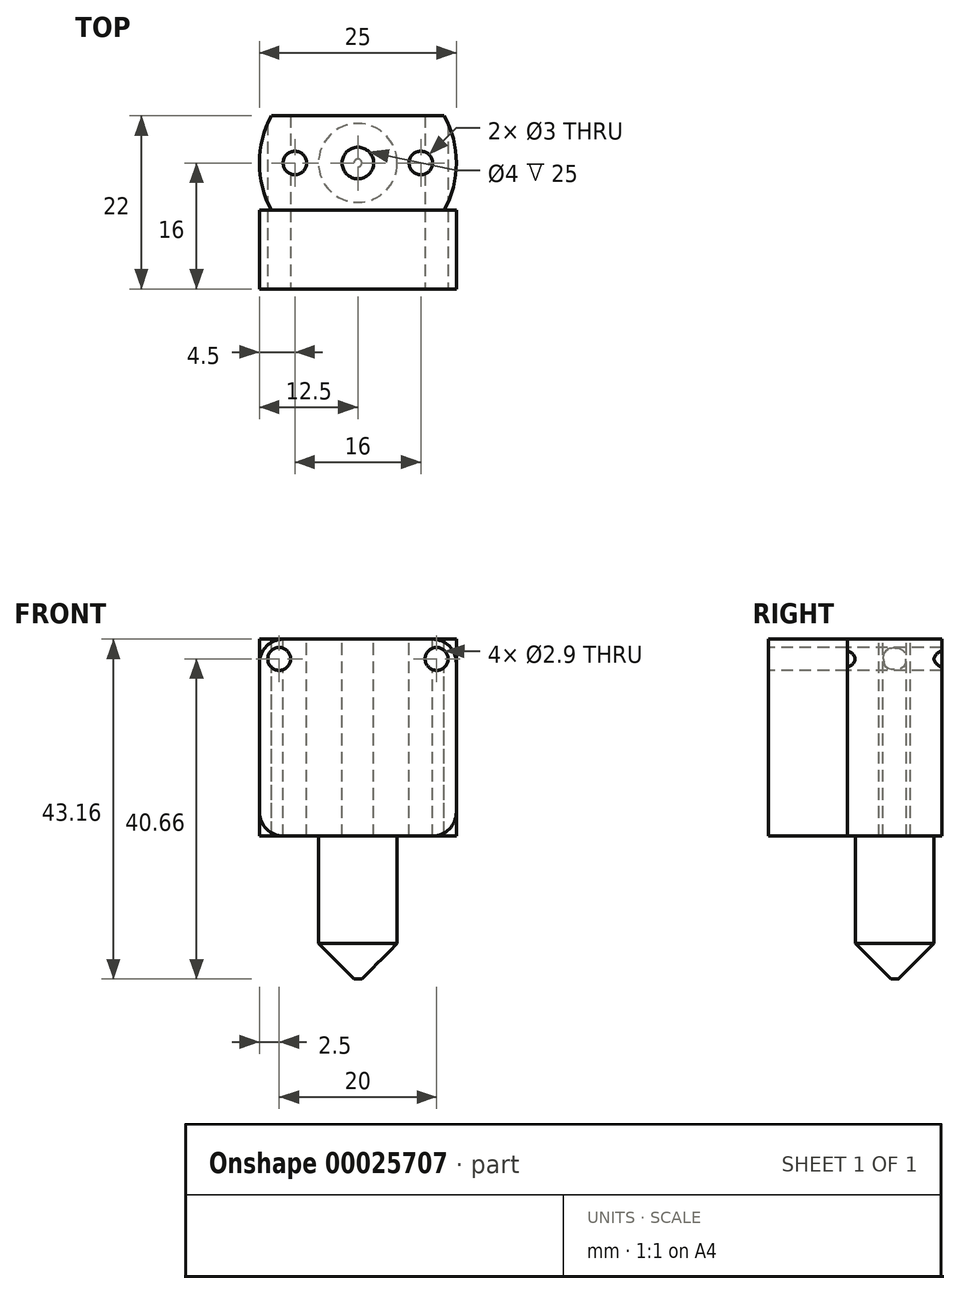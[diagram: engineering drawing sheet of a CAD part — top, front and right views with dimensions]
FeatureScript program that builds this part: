
annotation { "Feature Type Name" : "Feature", "Feature Type Description" : "" }
export const myFeature = defineFeature(function(context is Context, id is Id, definition is map)
    precondition{}
    {
        {
            var Q0;
            Q0=qCreatedBy(makeId("Front.planeOp"),FACE);
            var sketch = newSketch(context, id + "F0", { "sketchPlane" : qUnion([Q0])});
            skLineSegment(sketch, "E0.bottom", {"start": v(12.5, 0) * mm, "end": v(-12.5, 0) * mm});
            skLineSegment(sketch, "E0.top", {"start": v(12.5, -25) * mm, "end": v(-12.5, -25) * mm});
            skLineSegment(sketch, "E0.left", {"start": v(12.5, 0) * mm, "end": v(12.5, -25) * mm});
            skLineSegment(sketch, "E0.right", {"start": v(-12.5, 0) * mm, "end": v(-12.5, -25) * mm});
            skPoint(sketch, "E0.middle", {"position": v(0, -12.5) * mm});
            skSolve(sketch);
        }
        {
            var Q0;
            Q0 = qSketchRegion(id + "F0", true);
            extrude(context, id + "F1", {"entities" : qUnion([Q0]), "depth" : 12 * mm, "symmetric" : true});
        }
        {
            var Q0;
            Q0=qCreatedBy(makeId("Front.planeOp"),FACE);
            var sketch = newSketch(context, id + "F2", { "sketchPlane" : qUnion([Q0])});
            skLineSegment(sketch, "E1", {"start": v(0, -25) * mm, "end": v(0, -43.16) * mm});
            skLineSegment(sketch, "E2", {"start": v(0, -43.16) * mm, "end": v(0.5, -43.16) * mm});
            skLineSegment(sketch, "E3", {"start": v(0.5, -43.16) * mm, "end": v(5, -38.66) * mm});
            skLineSegment(sketch, "E4", {"start": v(5, -38.66) * mm, "end": v(5, -25) * mm});
            skLineSegment(sketch, "E5", {"start": v(5, -25) * mm, "end": v(0, -25) * mm});
            skSolve(sketch);
        }
        {
            var Q0;
            Q0 = qSketchRegion(id + "F2", true);
            var Q1;
            Q1=sQuery(id+"F2.wireOp",EDGE,"E1");
            revolve(context, id + "F3", {"operationType" : NewBodyOperationType.ADD, "entities" : qUnion([Q0]), "axis" : qUnion([Q1]), "revolveType" : RevolveType.FULL});
        }
        {
            var Q0;
            Q0=makeQuery(id+"F1.opExtrude","SWEPT_FACE",FACE,{"disambiguationData":[OSD([sQuery(id+"F0.wireOp",EDGE,"E0.bottom")])]});
            var sketch = newSketch(context, id + "F4", { "sketchPlane" : qUnion([Q0])});
            skCircle(sketch, "E6", {"center": v(0, 0) * mm, "radius": 2 * mm});
            skCircle(sketch, "E7", {"center": v(-8, 0) * mm, "radius": 1.5 * mm});
            skCircle(sketch, "E8", {"center": v(8, 0) * mm, "radius": 1.5 * mm});
            skLineSegment(sketch, "E9", {"start": v(-8, 0) * mm, "end": v(0, 0) * mm, "construction": true});
            skLineSegment(sketch, "E10", {"start": v(8, 0) * mm, "end": v(0, 0) * mm, "construction": true});
            skCircle(sketch, "E11", {"center": v(0, 0) * mm, "radius": 12.5 * mm});
            skCircle(sketch, "E12", {"center": v(0, 0) * mm, "radius": 26.2 * mm});
            skSolve(sketch);
        }
        {
            var Q0;
            Q0=makeQuery(id+"F4.imprint","IMPRINT",FACE,{"disambiguationData":[TD([[makeQuery(id+"F4.imprint","IMPRINT",EDGE,{"derivedFrom":sQuery(id+"F4.wireOp",EDGE,"E7")}),1.0]])]});
            var Q1;
            Q1=makeQuery(id+"F4.imprint","IMPRINT",FACE,{"disambiguationData":[TD([[makeQuery(id+"F4.imprint","IMPRINT",EDGE,{"derivedFrom":sQuery(id+"F4.wireOp",EDGE,"E6")}),1.0]])]});
            var Q2;
            Q2=makeQuery(id+"F4.imprint","IMPRINT",FACE,{"disambiguationData":[TD([[makeQuery(id+"F4.imprint","IMPRINT",EDGE,{"derivedFrom":sQuery(id+"F4.wireOp",EDGE,"E8")}),1.0]])]});
            var Q3;
            Q3=makeQuery(id+"F4.imprint","IMPRINT",FACE,{"disambiguationData":[TD([[makeQuery(id+"F4.imprint","IMPRINT",EDGE,{"derivedFrom":sQuery(id+"F4.wireOp",EDGE,"E12")}),1.0]])]});
            var Q4;
            {var subQ0=sQuery(id+"F4.wireOp",EDGE,"E11");var subQ1=sQuery(id+"F0.wireOp",EDGE,"E0.bottom");var subQ4=makeQuery(id+"F1.opExtrude","CAP_EDGE",EDGE,{"disambiguationData":[OSD([subQ1])],"isStart":false});var subQ5=makeQuery(id+"F4.imprint","INTERSECT",VERTEX,{"disambiguationData":[OD(1.0)],"derivedFrom":[subQ4,subQ0]});Q4=makeQuery(id+"F4.imprint","IMPRINT",FACE,{"disambiguationData":[TD([[makeQuery(id+"F4.imprint","IMPRINT",EDGE,{"disambiguationData":[TD([[subQ5,-1.0]])],"derivedFrom":subQ0}),-1.0]])]});}
            var Q5;
            {var subQ0=sQuery(id+"F4.wireOp",EDGE,"E11");var subQ1=sQuery(id+"F0.wireOp",EDGE,"E0.bottom");var subQ2=makeQuery(id+"F1.opExtrude","CAP_EDGE",EDGE,{"disambiguationData":[OSD([subQ1])],"isStart":true});var subQ3=makeQuery(id+"F4.imprint","INTERSECT",VERTEX,{"disambiguationData":[OD(0.0)],"derivedFrom":[subQ2,subQ0]});Q5=makeQuery(id+"F4.imprint","IMPRINT",FACE,{"disambiguationData":[TD([[makeQuery(id+"F4.imprint","IMPRINT",EDGE,{"disambiguationData":[TD([[subQ3,1.0]])],"derivedFrom":subQ0}),-1.0]])]});}
            var Q6;
            {var subQ0=sQuery(id+"F4.wireOp",EDGE,"E11");var subQ1=sQuery(id+"F0.wireOp",EDGE,"E0.bottom");var subQ2=makeQuery(id+"F1.opExtrude","CAP_EDGE",EDGE,{"disambiguationData":[OSD([subQ1])],"isStart":true});var subQ3=makeQuery(id+"F4.imprint","INTERSECT",VERTEX,{"disambiguationData":[OD(1.0)],"derivedFrom":[subQ2,subQ0]});Q6=makeQuery(id+"F4.imprint","IMPRINT",FACE,{"disambiguationData":[TD([[makeQuery(id+"F4.imprint","IMPRINT",EDGE,{"disambiguationData":[TD([[subQ3,-1.0]])],"derivedFrom":subQ0}),-1.0]])]});}
            var Q7;
            {var subQ0=sQuery(id+"F4.wireOp",EDGE,"E11");var subQ1=sQuery(id+"F0.wireOp",EDGE,"E0.bottom");var subQ4=makeQuery(id+"F1.opExtrude","CAP_EDGE",EDGE,{"disambiguationData":[OSD([subQ1])],"isStart":false});var subQ5=makeQuery(id+"F4.imprint","INTERSECT",VERTEX,{"disambiguationData":[OD(0.0)],"derivedFrom":[subQ4,subQ0]});Q7=makeQuery(id+"F4.imprint","IMPRINT",FACE,{"disambiguationData":[TD([[makeQuery(id+"F4.imprint","IMPRINT",EDGE,{"disambiguationData":[TD([[subQ5,1.0]])],"derivedFrom":subQ0}),-1.0]])]});}
            extrude(context, id + "F5", {"entities" : qUnion([Q0, Q1, Q2, Q3, Q4, Q5, Q6, Q7]), "operationType" : NewBodyOperationType.REMOVE, "oppositeDirection" : true, "depth" : 25 * mm});
        }
        {
            var Q0;
            Q0=makeQuery(id+"F1.opExtrude","CAP_FACE",FACE,{"disambiguationData":[OSD([sQuery(id+"F0.wireOp",EDGE,"E0.bottom"),sQuery(id+"F0.wireOp",EDGE,"E0.top"),sQuery(id+"F0.wireOp",EDGE,"E0.left"),sQuery(id+"F0.wireOp",EDGE,"E0.right")])],"isStart":false});
            var sketch = newSketch(context, id + "F6", { "sketchPlane" : qUnion([Q0])});
            skLineSegment(sketch, "E13.0", {"start": v(12.5, 0) * mm, "end": v(-12.5, 0) * mm});
            skLineSegment(sketch, "E13.1", {"start": v(-12.5, 0) * mm, "end": v(-12.5, -25) * mm});
            skLineSegment(sketch, "E13.2", {"start": v(12.5, 0) * mm, "end": v(12.5, -25) * mm});
            skLineSegment(sketch, "E13.3", {"start": v(12.5, -25) * mm, "end": v(-12.5, -25) * mm});
            skSolve(sketch);
        }
        {
            var Q0;
            {var subQ2=sQuery(id+"F6.wireOp",EDGE,"E13.1");Q0=makeQuery(id+"F6.imprint","IMPRINT",FACE,{"disambiguationData":[TD([[makeQuery(id+"F6.imprint","IMPRINT",EDGE,{"derivedFrom":subQ2}),1.0]])]});}
            var Q1;
            {var subQ1=makeQuery(id+"F5.opExtrude","SWEPT_FACE",FACE,{"disambiguationData":[OSD([sQuery(id+"F4.wireOp",EDGE,"E11")])]});var subQ2=makeQuery(id+"F1.opExtrude","CAP_FACE",FACE,{"disambiguationData":[OSD([sQuery(id+"F0.wireOp",EDGE,"E0.bottom"),sQuery(id+"F0.wireOp",EDGE,"E0.top"),sQuery(id+"F0.wireOp",EDGE,"E0.left"),sQuery(id+"F0.wireOp",EDGE,"E0.right")])],"isStart":false});var subQ3=makeQuery(id+"F5.boolean.opBoolean","INTERSECT",EDGE,{"disambiguationData":[OD(0.0)],"derivedFrom":[subQ2,subQ1]});Q1=makeQuery(id+"F6.imprint","IMPRINT",FACE,{"disambiguationData":[TD([[makeQuery(id+"F6.imprint","IMPRINT",EDGE,{"derivedFrom":subQ3}),1.0]])]});}
            var Q2;
            {var subQ2=sQuery(id+"F6.wireOp",EDGE,"E13.2");Q2=makeQuery(id+"F6.imprint","IMPRINT",FACE,{"disambiguationData":[TD([[makeQuery(id+"F6.imprint","IMPRINT",EDGE,{"derivedFrom":subQ2}),-1.0]])]});}
            extrude(context, id + "F7", {"entities" : qUnion([Q0, Q1, Q2]), "depth" : 10 * mm});
        }
        {
            var Q0;
            Q0=makeQuery(id+"F7.opExtrude","CAP_FACE",FACE,{"disambiguationData":[OSD([sQuery(id+"F6.wireOp",EDGE,"E13.0"),sQuery(id+"F6.wireOp",EDGE,"E13.1"),sQuery(id+"F6.wireOp",EDGE,"E13.2"),sQuery(id+"F6.wireOp",EDGE,"E13.3")])],"isStart":false});
            var sketch = newSketch(context, id + "F8", { "sketchPlane" : qUnion([Q0])});
            skLineSegment(sketch, "E14.bottom", {"start": v(10, -2.5) * mm, "end": v(-10, -2.5) * mm, "construction": true});
            skLineSegment(sketch, "E14.top", {"start": v(10, -22.5) * mm, "end": v(-10, -22.5) * mm, "construction": true});
            skLineSegment(sketch, "E14.left", {"start": v(10, -2.5) * mm, "end": v(10, -22.5) * mm, "construction": true});
            skLineSegment(sketch, "E14.right", {"start": v(-10, -2.5) * mm, "end": v(-10, -22.5) * mm, "construction": true});
            skPoint(sketch, "E14.middle", {"position": v(0, -12.5) * mm});
            skLineSegment(sketch, "E15", {"start": v(-12.5, -25) * mm, "end": v(12.5, 0) * mm, "construction": true});
            skCircle(sketch, "E16", {"center": v(-10, -2.5) * mm, "radius": 1.45 * mm});
            skCircle(sketch, "E17", {"center": v(10, -2.5) * mm, "radius": 1.45 * mm});
            skSolve(sketch);
        }
        {
            var Q0;
            Q0 = qSketchRegion(id + "F8", true);
            extrude(context, id + "F9", {"entities" : qUnion([Q0]), "operationType" : NewBodyOperationType.REMOVE, "oppositeDirection" : true, "depth" : 25 * mm});
        }
        {
            var Q0;
            Q0=makeQuery(id+"F7.opExtrude","SWEPT_EDGE",EDGE,{"disambiguationData":[OSD([sQuery(id+"F6.wireOp",EDGE,"E13.0"),sQuery(id+"F6.wireOp",EDGE,"E13.2")])]});
            var Q1;
            Q1=makeQuery(id+"F7.opExtrude","SWEPT_EDGE",EDGE,{"disambiguationData":[OSD([sQuery(id+"F6.wireOp",EDGE,"E13.0"),sQuery(id+"F6.wireOp",EDGE,"E13.1")])]});
            var Q2;
            Q2=makeQuery(id+"F7.opExtrude","SWEPT_EDGE",EDGE,{"disambiguationData":[OSD([sQuery(id+"F6.wireOp",EDGE,"E13.1"),sQuery(id+"F6.wireOp",EDGE,"E13.3")])]});
            var Q3;
            Q3=makeQuery(id+"F7.opExtrude","SWEPT_EDGE",EDGE,{"disambiguationData":[OSD([sQuery(id+"F6.wireOp",EDGE,"E13.2"),sQuery(id+"F6.wireOp",EDGE,"E13.3")])]});
            fillet(context, id + "F10", {"entities" : qUnion([Q0, Q1, Q2, Q3]), "radius" : 3 * mm, "tangentPropagation" : true, "allowEdgeOverflow" : false});
        }
    });
